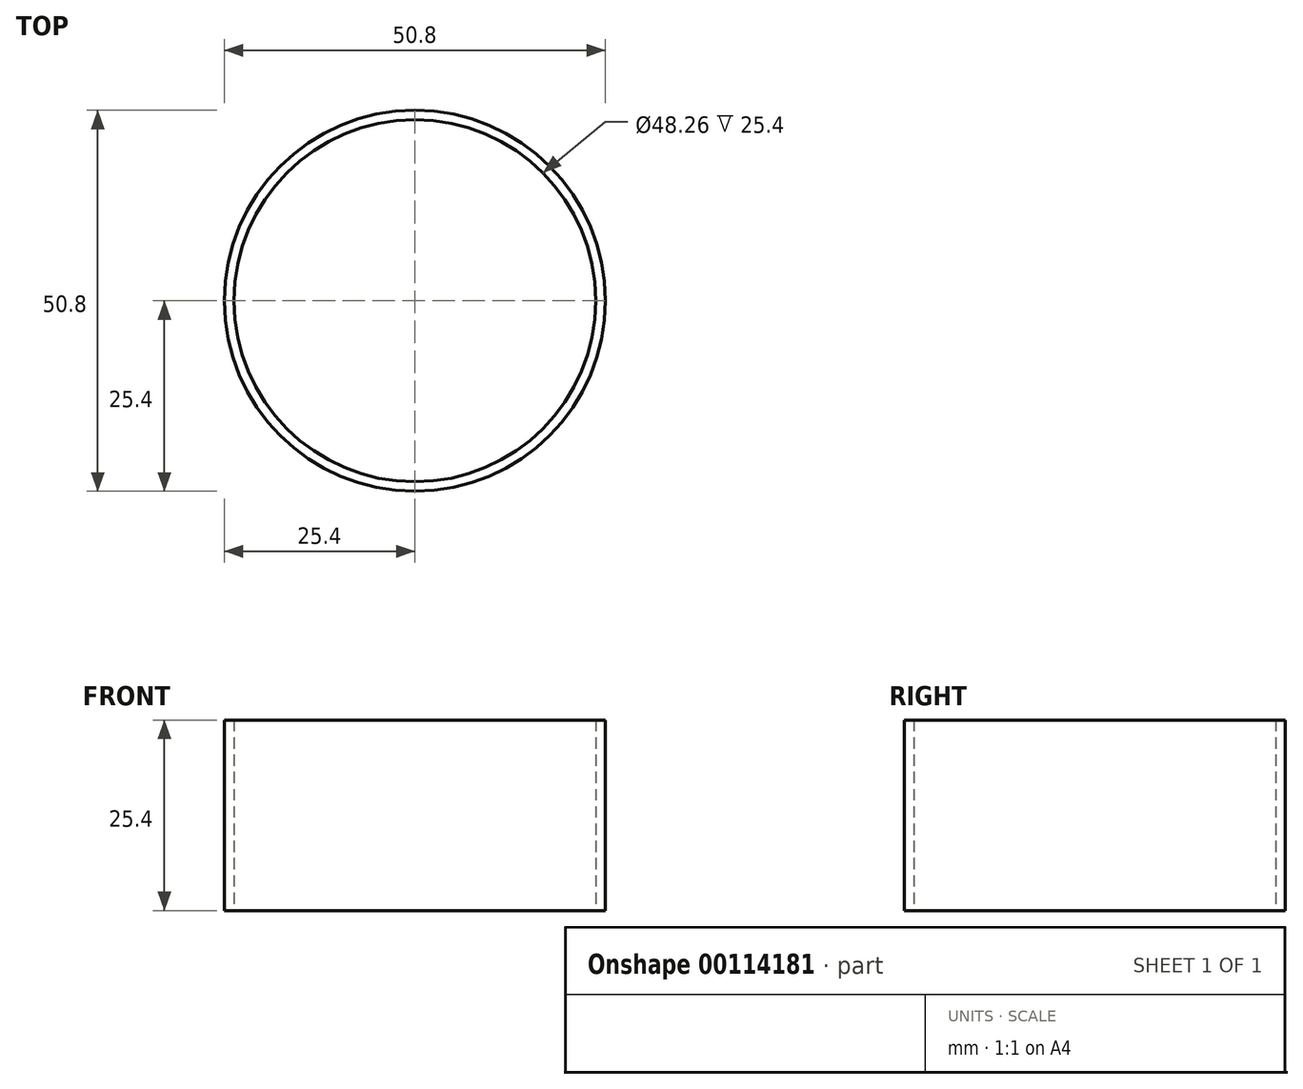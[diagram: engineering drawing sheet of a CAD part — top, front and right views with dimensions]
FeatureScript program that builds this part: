
annotation { "Feature Type Name" : "Feature", "Feature Type Description" : "" }
export const myFeature = defineFeature(function(context is Context, id is Id, definition is map)
    precondition{}
    {
        {
            var Q0;
            Q0=qCreatedBy(makeId("Top.planeOp"),FACE);
            var sketch = newSketch(context, id + "F0", { "sketchPlane" : qUnion([Q0])});
            skCircle(sketch, "E0", {"center": v(0, 0) * mm, "radius": 25.4 * mm});
            skCircle(sketch, "E1", {"center": v(0, 0) * mm, "radius": 24.13 * mm});
            skSolve(sketch);
        }
        {
            var Q0;
            Q0 = qSketchRegion(id + "F0", true);
            extrude(context, id + "F1", {"entities" : qUnion([Q0]), "depth" : 25.4 * mm});
        }
    });
